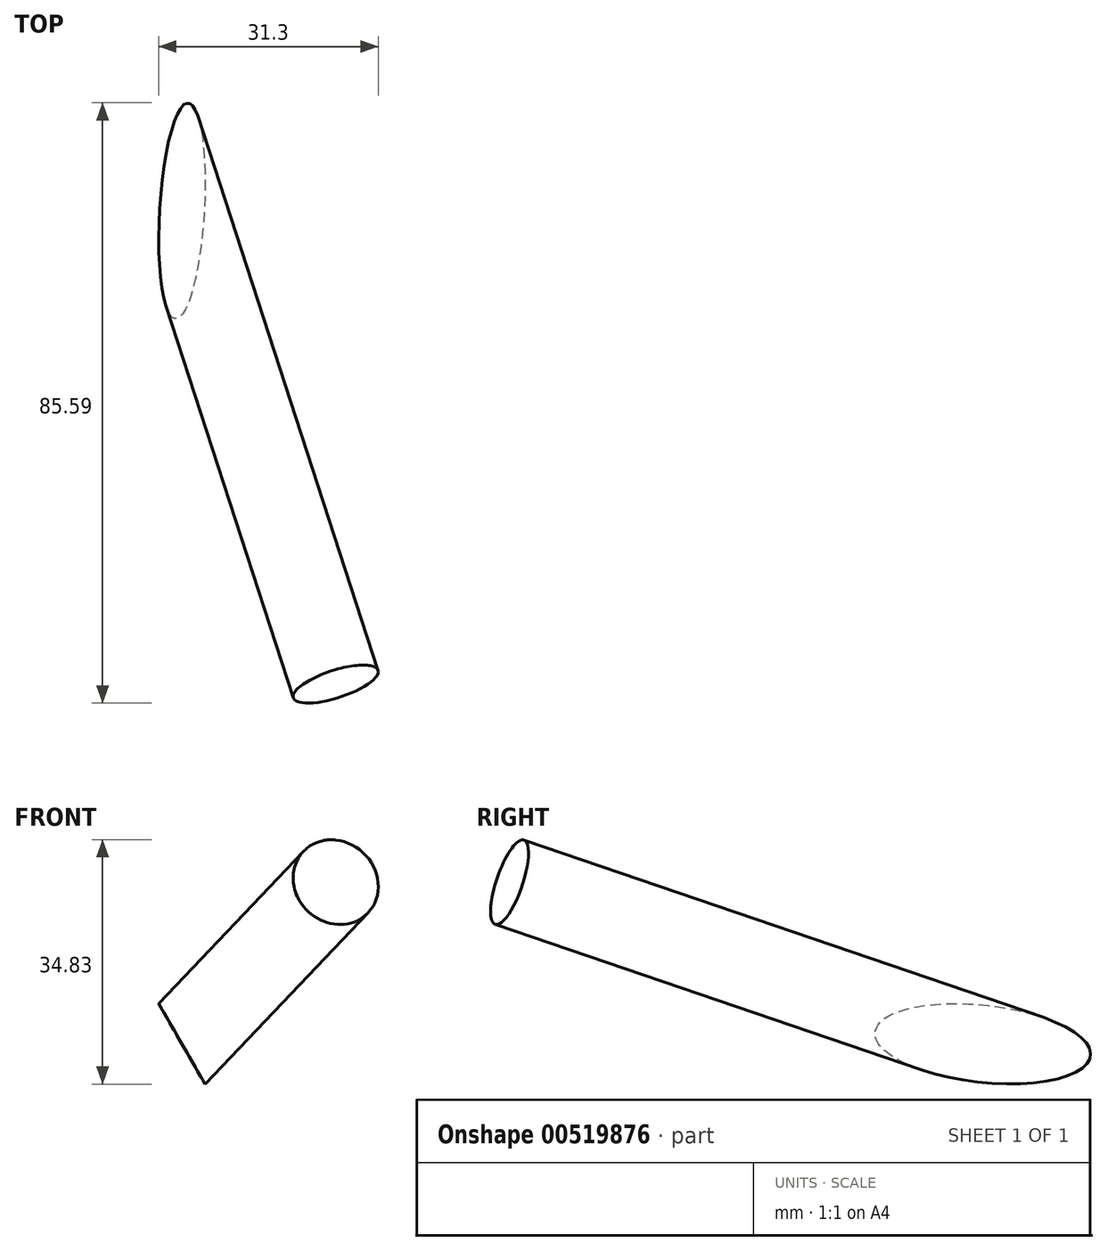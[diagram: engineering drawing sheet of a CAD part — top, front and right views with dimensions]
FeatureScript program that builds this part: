
annotation { "Feature Type Name" : "Feature", "Feature Type Description" : "" }
export const myFeature = defineFeature(function(context is Context, id is Id, definition is map)
    precondition{}
    {
        {
            var Q0;
            Q0=qCreatedBy(makeId("Front.planeOp"),FACE);
            var sketch = newSketch(context, id + "F0", { "sketchPlane" : qUnion([Q0])});
            skPoint(sketch, "E0", {"position": v(0, 48.46) * mm});
            skPoint(sketch, "E1", {"position": v(27.98, 0) * mm});
            skLineSegment(sketch, "E2", {"start": v(0, 48.46) * mm, "end": v(27.98, 0) * mm, "construction": true});
            skSolve(sketch);
        }
        {
            var Q0;
            Q0=sQuery(id+"F0.wireOp",EDGE,"E2");
            cPlane(context, id + "F1", {"entities" : qUnion([Q0]), "cplaneType" : CPlaneType.LINE_ANGLE, "offset" : 25.4 * mm, "angle" : 0 * degree, "width" : 152.4 * mm, "height" : 152.4 * mm});
        }
        {
            var Q0;
            Q0=qCreatedBy(makeId("Top.planeOp"),FACE);
            var sketch = newSketch(context, id + "F2", { "sketchPlane" : qUnion([Q0])});
            skPoint(sketch, "E3", {"position": v(50.55, -79.9) * mm});
            skPoint(sketch, "E4", {"position": v(26.94, -87.56) * mm});
            skLineSegment(sketch, "E5", {"start": v(26.94, -87.56) * mm, "end": v(50.55, -79.9) * mm, "construction": true});
            skSolve(sketch);
        }
        {
            var Q0;
            Q0=sQuery(id+"F2.wireOp",EDGE,"E5");
            cPlane(context, id + "F3", {"entities" : qUnion([Q0]), "cplaneType" : CPlaneType.LINE_ANGLE, "offset" : 25.4 * mm, "angle" : 18 * degree, "oppositeDirection" : true, "width" : 152.4 * mm, "height" : 152.4 * mm});
        }
        {
            var Q0;
            Q0=qCreatedBy(id+"F3.planeOp",FACE);
            var sketch = newSketch(context, id + "F4", { "sketchPlane" : qUnion([Q0])});
            skCircle(sketch, "E6", {"center": v(-6.79, 29.2) * mm, "radius": 6.35 * mm});
            skSolve(sketch);
        }
        {
            var Q0;
            Q0 = qSketchRegion(id + "F4", true);
            var Q1;
            Q1=qCreatedBy(id+"F1.planeOp",FACE);
            extrude(context, id + "F5", {"entities" : qUnion([Q0]), "endBound" : BoundingType.UP_TO_SURFACE, "depth" : 25.4 * mm, "endBoundEntityFace" : qUnion([Q1]), "offsetDistance" : 25.4 * mm});
        }
        {
            var Q0;
            Q0=makeQuery(id+"F5.opExtrude","CAP_FACE",FACE,{"disambiguationData":[OSD([sQuery(id+"F4.wireOp",EDGE,"E6")])],"isStart":false});
            var sketch = newSketch(context, id + "F6", { "sketchPlane" : qUnion([Q0])});
            skPoint(sketch, "E7", {"position": v(0, 21.63) * mm});
            skLineSegment(sketch, "E8", {"start": v(7.38, 16.83) * mm, "end": v(-7.38, 26.43) * mm, "construction": true});
            skLineSegment(sketch, "E9", {"start": v(7.38, 16.83) * mm, "end": v(7.38, 28.06) * mm, "construction": true});
            skLineSegment(sketch, "E10", {"start": v(-7.38, 26.43) * mm, "end": v(-7.38, 15.2) * mm, "construction": true});
            skPoint(sketch, "E11.startSnap0", {"position": v(-15.39, 19.58) * mm});
            skPoint(sketch, "E11.endSnap0", {"position": v(15.39, 23.68) * mm});
            skEllipse(sketch, "E12", {"center": v(0, 21.63) * mm, "majorRadius": 10.12 * mm, "minorRadius": 3.07 * mm, "majorAxis": v(-1, -0.13)});
            skPoint(sketch, "E13", {"position": v(-7.38, 20.65) * mm});
            skPoint(sketch, "E14", {"position": v(0.4, 18.61) * mm});
            skPoint(sketch, "E15", {"position": v(-0.84, 27.93) * mm});
            skPoint(sketch, "E16", {"position": v(0, 15.23) * mm});
            skLineSegment(sketch, "E17", {"start": v(-0.84, 27.93) * mm, "end": v(0, 15.23) * mm, "construction": true});
            skLineSegment(sketch, "E18", {"start": v(-15.39, 19.58) * mm, "end": v(15.39, 23.68) * mm, "construction": true});
            skLineSegment(sketch, "E19", {"start": v(-0.84, 27.93) * mm, "end": v(15.39, 23.68) * mm, "construction": true});
            skLineSegment(sketch, "E20", {"start": v(-7.38, 20.65) * mm, "end": v(0.4, 18.61) * mm, "construction": true});
            skSolve(sketch);
        }
    });
